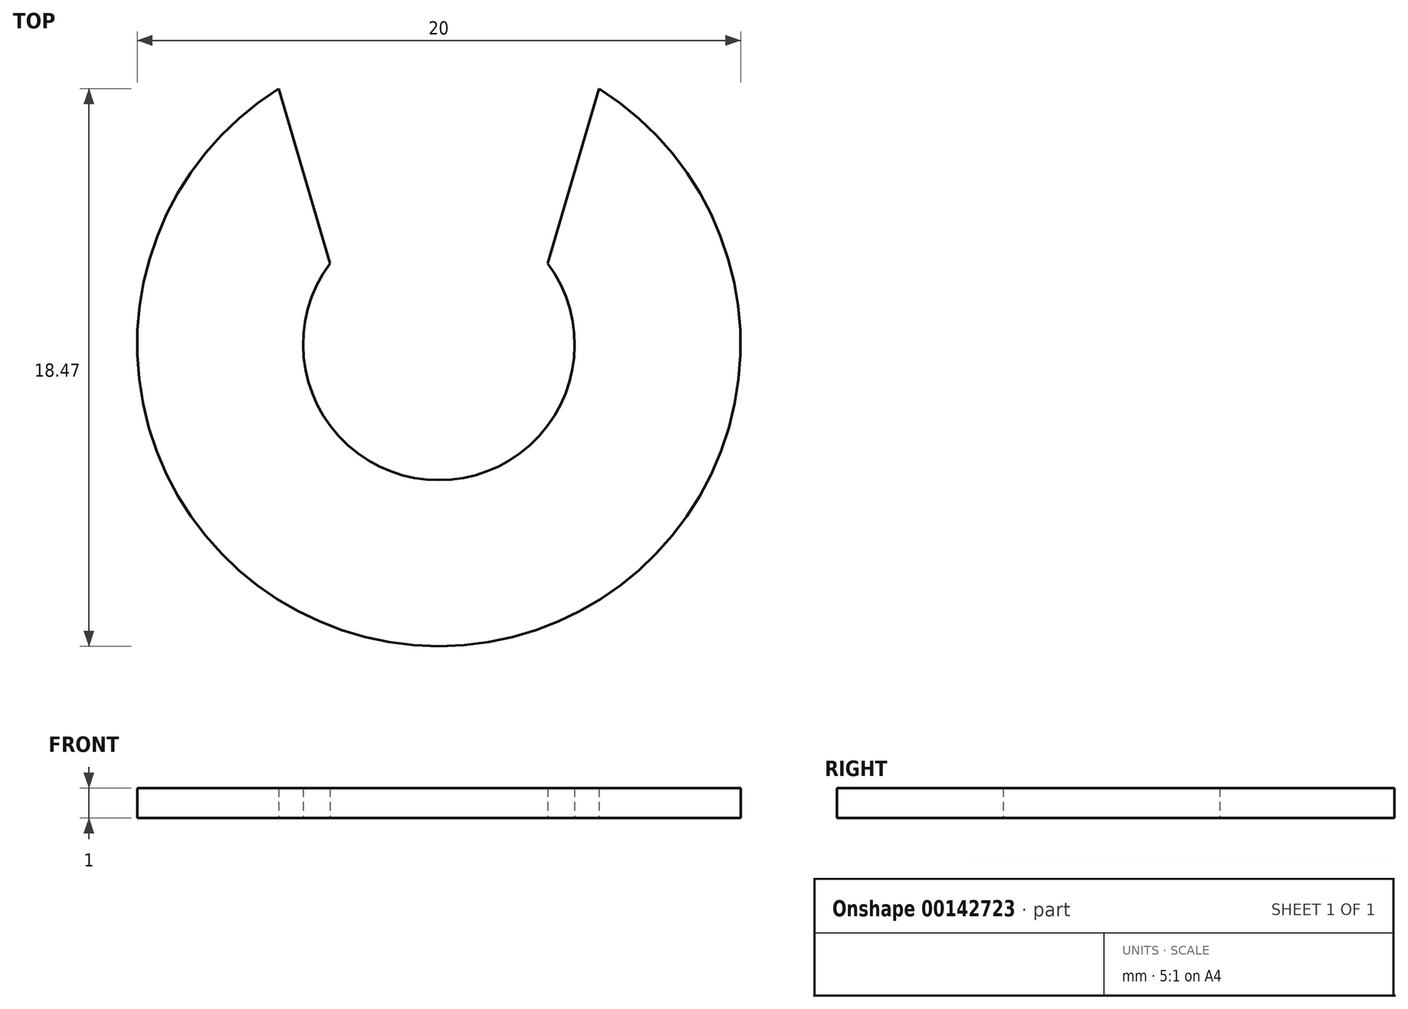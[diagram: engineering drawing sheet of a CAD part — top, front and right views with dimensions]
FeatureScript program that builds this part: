
annotation { "Feature Type Name" : "Feature", "Feature Type Description" : "" }
export const myFeature = defineFeature(function(context is Context, id is Id, definition is map)
    precondition{}
    {
        {
            var Q0;
            Q0=qCreatedBy(makeId("Top.planeOp"),FACE);
            var sketch = newSketch(context, id + "F0", { "sketchPlane" : qUnion([Q0])});
            skArc(sketch, "E0", {"start": v(-3.61, 2.69) * mm, "mid": v(0, -4.5) * mm, "end": v(3.61, 2.69) * mm});
            skArc(sketch, "E1", {"start": v(-5.31, 8.47) * mm, "mid": v(0, -10) * mm, "end": v(5.31, 8.47) * mm});
            skLineSegment(sketch, "E2", {"start": v(-5.31, 8.47) * mm, "end": v(-3.61, 2.69) * mm});
            skPoint(sketch, "E3", {"position": v(-4.94, 7.21) * mm});
            skLineSegment(sketch, "E4.MirrorCS", {"start": v(5.31, 8.47) * mm, "end": v(3.61, 2.69) * mm});
            skPoint(sketch, "E5.MirrorP", {"position": v(4.94, 7.21) * mm});
            skPoint(sketch, "E6.orphan", {"position": v(-2.82, 0) * mm});
            skPoint(sketch, "E7.orphan", {"position": v(2.82, 0) * mm});
            skSolve(sketch);
        }
        {
            var Q0;
            Q0=makeQuery(id+"F0.imprint","IMPRINT",FACE,{"disambiguationData":[TD([[makeQuery(id+"F0.imprint","IMPRINT",EDGE,{"derivedFrom":sQuery(id+"F0.wireOp",EDGE,"E0")}),-1.0]])]});
            extrude(context, id + "F1", {"entities" : qUnion([Q0]), "depth" : 1 * mm});
        }
    });
